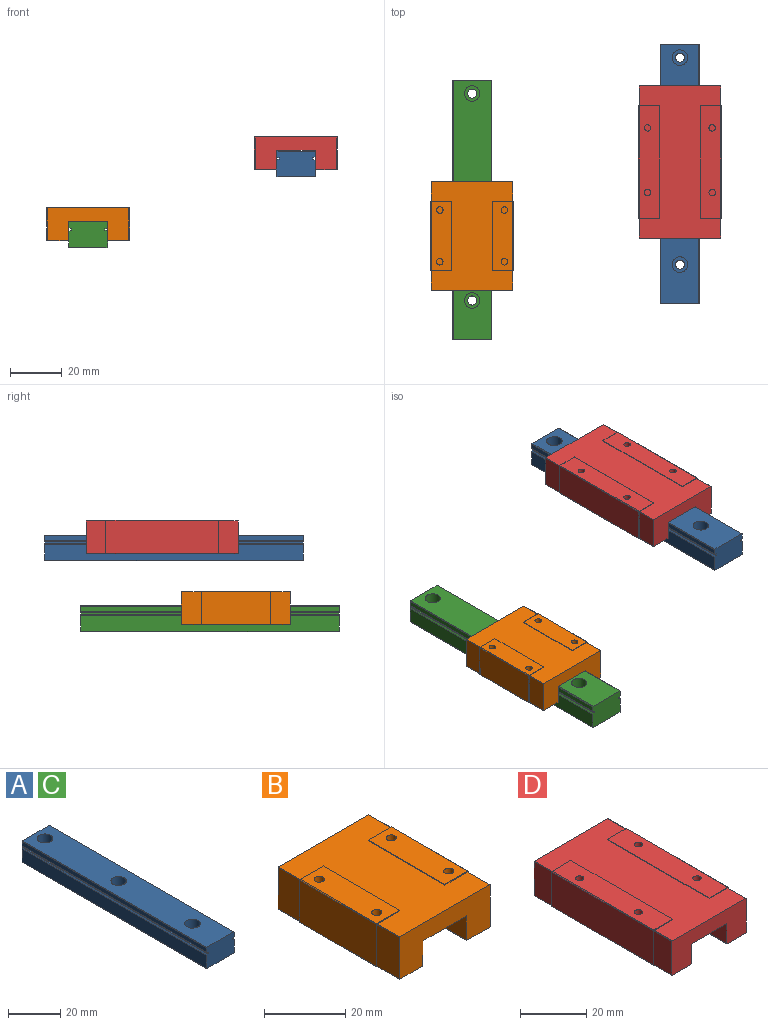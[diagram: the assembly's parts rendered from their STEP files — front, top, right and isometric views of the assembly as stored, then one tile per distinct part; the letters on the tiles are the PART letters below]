
ASSEMBLY  parts=4 mates=2
PART A: 31 faces, bbox 15x100x10 mm
  f0: plane 100x0.5mm, normal (0,0,1), area 50mm2, adj f1,f19,f20,f21
  f1: plane 100x0.5mm, normal (1,0,0), area 50mm2, adj f0,f2,f20,f21
  f2: plane 100x0.5mm, normal (0,0,-1), area 50mm2, adj f1,f3,f20,f21
  f3: plane 100x0.5mm, normal (0.71,0,-0.71), area 70.7mm2, adj f2,f4,f20,f21
  f4: plane 100x2mm, normal (1,0,0), area 200mm2, adj f3,f5,f20,f21
  f5: plane 100x0.2mm, normal (0.71,0,0.71), area 28.3mm2, adj f4,f6,f20,f21
  f6: plane 100x14.6mm, normal (0,0,1), area 1375.2mm2, adj f5,f7,f20,f21,f25,f27,f29
  f7: plane 100x0.2mm, normal (-0.71,0,0.71), area 28.3mm2, adj f6,f8,f20,f21
  f8: plane 100x2mm, normal (-1,0,0), area 200mm2, adj f7,f9,f20,f21
  f9: plane 100x0.5mm, normal (-0.71,0,-0.71), area 70.7mm2, adj f8,f10,f20,f21
  f10: plane 100x0.5mm, normal (0,0,-1), area 50mm2, adj f9,f11,f20,f21
  f11: plane 100x0.5mm, normal (-1,0,0), area 50mm2, adj f10,f12,f20,f21
  f12: plane 100x0.5mm, normal (0,0,1), area 50mm2, adj f11,f13,f20,f21
  f13: plane 100x0.5mm, normal (-0.71,0,0.71), area 70.7mm2, adj f12,f14,f20,f21
  f14: plane 100x6.1mm, normal (-1,0,0), area 610mm2, adj f13,f15,f20,f21
  f15: plane 100x0.2mm, normal (-0.71,0,-0.71), area 28.3mm2, adj f14,f16,f20,f21
  f16: plane 100x14.6mm, normal (0,0,-1), area 1431.1mm2, adj f15,f17,f20,f21,f22,f23,f24
  f17: plane 100x0.2mm, normal (0.71,0,-0.71), area 28.3mm2, adj f16,f18,f20,f21
  f18: plane 100x6.1mm, normal (1,0,0), area 610mm2, adj f17,f19,f20,f21
  f19: plane 100x0.5mm, normal (0.71,0,0.71), area 70.7mm2, adj f0,f18,f20,f21
  f20: plane 15x10mm, normal (0,-1,0), area 148.4mm2, adj f0,f1,f2,f3,f4,f5,f6,f7
  f21: plane 15x10mm, normal (0,1,0), area 148.4mm2, adj f0,f1,f2,f3,f4,f5,f6,f7
  f22: cylinder r=1.75mm len=5.5mm, axis (0,0,1), area 60.5mm2, adj f16,f30
  f23: cylinder r=1.75mm len=5.5mm, axis (0,0,1), area 60.5mm2, adj f16,f28
  f24: cylinder r=1.75mm len=5.5mm, axis (0,0,1), area 60.5mm2, adj f16,f26
  f25: cylinder r=3mm len=6mm, axis (0,0,1), area 84.8mm2, adj f6,f26
  f26: plane 6x6mm, normal (0,0,1), area 18.7mm2, adj f24,f25
  f27: cylinder r=3mm len=6mm, axis (0,0,1), area 84.8mm2, adj f6,f28
  f28: plane 6x6mm, normal (0,0,1), area 18.7mm2, adj f23,f27
  f29: cylinder r=3mm len=6mm, axis (0,0,1), area 84.8mm2, adj f6,f30
  f30: plane 6x6mm, normal (0,0,1), area 18.7mm2, adj f22,f29
PART B: 44 faces, bbox 32x42.1x13 mm
  f0: plane 26.7x8mm, normal (0,0,1), area 203.8mm2, adj f1,f2,f9,f34,f40,f42
  f1: plane 13x8.2mm, normal (0,-1,0), area 4.2mm2, adj f0,f3,f9,f10,f11,f21,f22,f23
  f2: plane 13x8.2mm, normal (0,1,0), area 4.2mm2, adj f0,f3,f9,f10,f11,f24,f29,f30
  f3: plane 42.1x8.1mm, normal (0,0,-1), area 337.9mm2, adj f1,f2,f4,f11,f12,f14,f21,f29
  f4: plane 31.6x12.8mm, normal (0,1,0), area 291.9mm2, adj f3,f13,f14,f15,f16,f17,f18,f24
  f5: plane 26.7x0.2mm, normal (0.71,0,-0.71), area 7.6mm2, adj f6,f13,f26,f33
  f6: plane 26.7x12.6mm, normal (1,0,0), area 336.4mm2, adj f5,f7,f26,f33
  f7: plane 26.7x0.2mm, normal (0.71,0,0.71), area 7.6mm2, adj f6,f8,f26,f33
  f8: plane 26.7x8mm, normal (0,0,1), area 203.8mm2, adj f7,f26,f33,f35,f36,f38
  f9: plane 26.7x0.2mm, normal (-0.71,0,0.71), area 7.6mm2, adj f0,f1,f2,f10
  f10: plane 26.7x12.6mm, normal (-1,0,0), area 336.4mm2, adj f1,f2,f9,f11
  f11: plane 26.7x0.2mm, normal (-0.71,0,-0.71), area 7.6mm2, adj f1,f2,f3,f10
  f12: plane 31.6x12.8mm, normal (0,-1,0), area 291.9mm2, adj f3,f13,f14,f15,f16,f17,f18,f19
  f13: plane 42.1x8.1mm, normal (0,0,-1), area 337.9mm2, adj f4,f5,f12,f18,f20,f26,f28,f33
  f14: plane 42.1x0.2mm, normal (0.71,0,-0.71), area 11.9mm2, adj f3,f4,f12,f15
  f15: plane 42.1x7.3mm, normal (1,0,0), area 307.3mm2, adj f4,f12,f14,f16
  f16: plane 42.1x15mm, normal (0,0,-1), area 631.5mm2, adj f4,f12,f15,f17
  f17: plane 42.1x7.3mm, normal (-1,0,0), area 307.3mm2, adj f4,f12,f16,f18
  f18: plane 42.1x0.2mm, normal (-0.71,0,-0.71), area 11.9mm2, adj f4,f12,f13,f17
  f19: plane 12.52x7.7mm, normal (1,0,0), area 96.4mm2, adj f12,f20,f25,f26
  f20: plane 7.7x0.2mm, normal (0.71,0,-0.71), area 2.2mm2, adj f12,f13,f19,f26
  f21: plane 7.7x0.2mm, normal (-0.71,0,-0.71), area 2.2mm2, adj f1,f3,f12,f22
  f22: plane 12.52x7.7mm, normal (-1,0,0), area 96.4mm2, adj f1,f12,f21,f23
  f23: plane 7.7x0.08mm, normal (-0.71,0,0.71), area 0.9mm2, adj f1,f12,f22,f24
  f24: plane 42.1x31.43mm, normal (0,0,1), area 900.6mm2, adj f1,f2,f4,f12,f23,f25,f26,f31
  f25: plane 7.7x0.08mm, normal (0.71,0,0.71), area 0.9mm2, adj f12,f19,f24,f26
  f26: plane 13x8.2mm, normal (0,-1,0), area 4.2mm2, adj f5,f6,f7,f8,f13,f19,f20,f24
  f27: plane 12.52x7.7mm, normal (1,0,0), area 96.4mm2, adj f4,f28,f32,f33
  f28: plane 7.7x0.2mm, normal (0.71,0,-0.71), area 2.2mm2, adj f4,f13,f27,f33
  f29: plane 7.7x0.2mm, normal (-0.71,0,-0.71), area 2.2mm2, adj f2,f3,f4,f30
  f30: plane 12.52x7.7mm, normal (-1,0,0), area 96.4mm2, adj f2,f4,f29,f31
  f31: plane 7.7x0.08mm, normal (-0.71,0,0.71), area 0.9mm2, adj f2,f4,f24,f30
  f32: plane 7.7x0.08mm, normal (0.71,0,0.71), area 0.9mm2, adj f4,f24,f27,f33
  f33: plane 13x8.2mm, normal (0,1,0), area 4.2mm2, adj f5,f6,f7,f8,f13,f24,f27,f28
  f34: plane 26.7x0.2mm, normal (1,0,0), area 5.3mm2, adj f0,f1,f2,f24
  f35: plane 26.7x0.2mm, normal (-1,0,0), area 5.3mm2, adj f8,f24,f26,f33
  f36: cylinder r=1.25mm len=4mm, axis (0,0,1), area 31.4mm2, adj f8,f37
  f37: plane 2.5x2.5mm, normal (0,0,1), area 4.9mm2, adj f36
  f38: cylinder r=1.25mm len=4mm, axis (0,0,1), area 31.4mm2, adj f8,f39
  f39: plane 2.5x2.5mm, normal (0,0,1), area 4.9mm2, adj f38
  f40: cylinder r=1.25mm len=4mm, axis (0,0,1), area 31.4mm2, adj f0,f41
  f41: plane 2.5x2.5mm, normal (0,0,1), area 4.9mm2, adj f40
  f42: cylinder r=1.25mm len=4mm, axis (0,0,1), area 31.4mm2, adj f0,f43
  f43: plane 2.5x2.5mm, normal (0,0,1), area 4.9mm2, adj f42
PART C: same geometry as A
PART D: 44 faces, bbox 32x58.8x13 mm
  f0: plane 13x8.2mm, normal (0,-1,0), area 4.2mm2, adj f2,f3,f8,f9,f10,f21,f22,f23
  f1: plane 13x8.2mm, normal (0,1,0), area 4.2mm2, adj f4,f5,f6,f7,f12,f24,f29,f30
  f2: plane 43.4x8mm, normal (0,0,1), area 337.4mm2, adj f0,f8,f33,f38,f40,f42
  f3: plane 58.8x8.1mm, normal (0,0,-1), area 473.2mm2, adj f0,f10,f11,f13,f18,f21,f28,f33
  f4: plane 43.4x0.2mm, normal (0.71,0,-0.71), area 12.3mm2, adj f1,f5,f12,f26
  f5: plane 43.4x12.6mm, normal (1,0,0), area 546.8mm2, adj f1,f4,f6,f26
  f6: plane 43.4x0.2mm, normal (0.71,0,0.71), area 12.3mm2, adj f1,f5,f7,f26
  f7: plane 43.4x8mm, normal (0,0,1), area 337.4mm2, adj f1,f6,f26,f34,f36,f43
  f8: plane 43.4x0.2mm, normal (-0.71,0,0.71), area 12.3mm2, adj f0,f2,f9,f33
  f9: plane 43.4x12.6mm, normal (-1,0,0), area 546.8mm2, adj f0,f8,f10,f33
  f10: plane 43.4x0.2mm, normal (-0.71,0,-0.71), area 12.3mm2, adj f0,f3,f9,f33
  f11: plane 31.6x12.8mm, normal (0,-1,0), area 291.9mm2, adj f3,f12,f13,f14,f15,f16,f17,f19
  f12: plane 58.8x8.1mm, normal (0,0,-1), area 473.2mm2, adj f1,f4,f11,f17,f18,f20,f26,f29
  f13: plane 58.8x0.2mm, normal (0.71,0,-0.71), area 16.6mm2, adj f3,f11,f14,f18
  f14: plane 58.8x7.3mm, normal (1,0,0), area 429.2mm2, adj f11,f13,f15,f18
  f15: plane 58.8x15mm, normal (0,0,-1), area 882mm2, adj f11,f14,f16,f18
  f16: plane 58.8x7.3mm, normal (-1,0,0), area 429.2mm2, adj f11,f15,f17,f18
  f17: plane 58.8x0.2mm, normal (-0.71,0,-0.71), area 16.6mm2, adj f11,f12,f16,f18
  f18: plane 31.6x12.8mm, normal (0,1,0), area 291.9mm2, adj f3,f12,f13,f14,f15,f16,f17,f24
  f19: plane 12.52x7.7mm, normal (1,0,0), area 96.4mm2, adj f11,f20,f25,f26
  f20: plane 7.7x0.2mm, normal (0.71,0,-0.71), area 2.2mm2, adj f11,f12,f19,f26
  f21: plane 7.7x0.2mm, normal (-0.71,0,-0.71), area 2.2mm2, adj f0,f3,f11,f22
  f22: plane 12.52x7.7mm, normal (-1,0,0), area 96.4mm2, adj f0,f11,f21,f23
  f23: plane 7.7x0.08mm, normal (-0.71,0,0.71), area 0.9mm2, adj f0,f11,f22,f24
  f24: plane 58.8x31.43mm, normal (0,0,1), area 1161.1mm2, adj f0,f1,f11,f18,f23,f25,f26,f31
  f25: plane 7.7x0.08mm, normal (0.71,0,0.71), area 0.9mm2, adj f11,f19,f24,f26
  f26: plane 13x8.2mm, normal (0,-1,0), area 4.2mm2, adj f4,f5,f6,f7,f12,f19,f20,f24
  f27: plane 12.52x7.7mm, normal (-1,0,0), area 96.4mm2, adj f18,f28,f32,f33
  f28: plane 7.7x0.2mm, normal (-0.71,0,-0.71), area 2.2mm2, adj f3,f18,f27,f33
  f29: plane 7.7x0.2mm, normal (0.71,0,-0.71), area 2.2mm2, adj f1,f12,f18,f30
  f30: plane 12.52x7.7mm, normal (1,0,0), area 96.4mm2, adj f1,f18,f29,f31
  f31: plane 7.7x0.08mm, normal (0.71,0,0.71), area 0.9mm2, adj f1,f18,f24,f30
  f32: plane 7.7x0.08mm, normal (-0.71,0,0.71), area 0.9mm2, adj f18,f24,f27,f33
  f33: plane 13x8.2mm, normal (0,1,0), area 4.2mm2, adj f2,f3,f8,f9,f10,f24,f27,f28
  f34: cylinder r=1.25mm len=4mm, axis (0,0,1), area 31.4mm2, adj f7,f35
  f35: plane 2.5x2.5mm, normal (0,0,1), area 4.9mm2, adj f34
  f36: cylinder r=1.25mm len=4mm, axis (0,0,1), area 31.4mm2, adj f7,f37
  f37: plane 2.5x2.5mm, normal (0,0,1), area 4.9mm2, adj f36
  f38: cylinder r=1.25mm len=4mm, axis (0,0,1), area 31.4mm2, adj f2,f39
  f39: plane 2.5x2.5mm, normal (0,0,1), area 4.9mm2, adj f38
  f40: cylinder r=1.25mm len=4mm, axis (0,0,1), area 31.4mm2, adj f2,f41
  f41: plane 2.5x2.5mm, normal (0,0,1), area 4.9mm2, adj f40
  f42: plane 43.4x0.2mm, normal (1,0,0), area 8.7mm2, adj f0,f2,f24,f33
  f43: plane 43.4x0.2mm, normal (-1,0,0), area 8.7mm2, adj f1,f7,f24,f26
PLACE A t=(26.3,24.31,15.75)mm fixed
PLACE B t=(1.67,-28.52,11.94)mm
PLACE C t=(-54.01,10.48,-11.64)mm fixed
PLACE D t=(35.37,8.34,39.33)mm
MATE slider C.f21 <-> B.f12  axis (0,1,0) through (-39.53,10.48,4.5)mm
MATE slider A.f21 <-> D.f11  axis (0,1,0) through (40.78,24.31,31.9)mm
